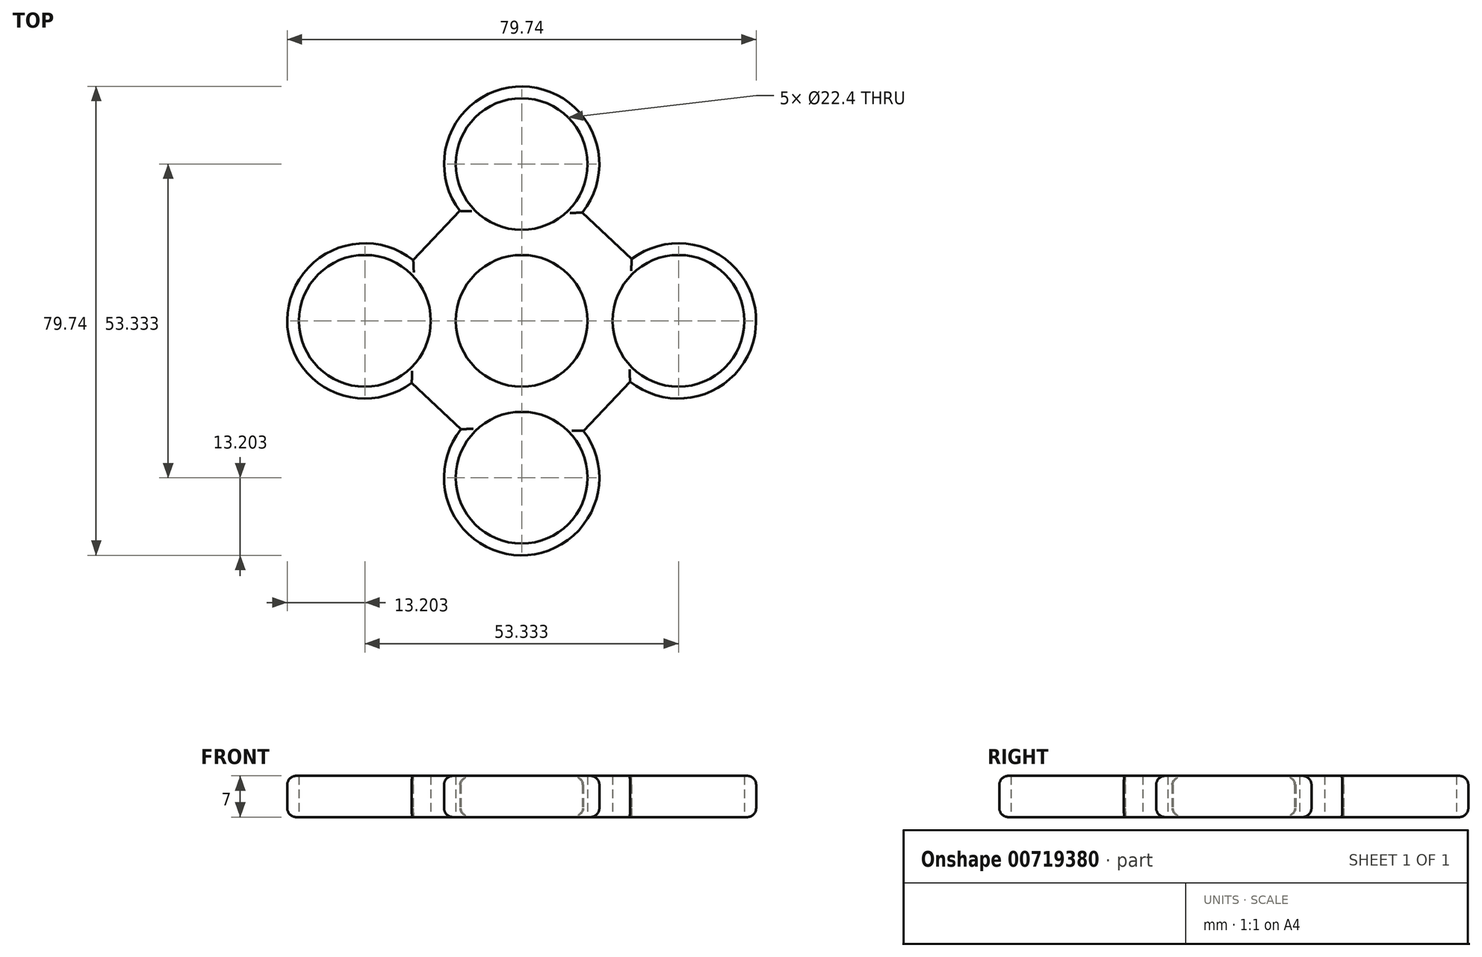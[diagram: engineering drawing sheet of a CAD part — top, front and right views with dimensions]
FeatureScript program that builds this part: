
annotation { "Feature Type Name" : "Feature", "Feature Type Description" : "" }
export const myFeature = defineFeature(function(context is Context, id is Id, definition is map)
    precondition{}
    {
        {
            var Q0;
            Q0=qCreatedBy(makeId("Top.planeOp"),FACE);
            var sketch = newSketch(context, id + "F0", { "sketchPlane" : qUnion([Q0])});
            skCircle(sketch, "E0", {"center": v(0, 0) * mm, "radius": 11.2 * mm});
            skCircle(sketch, "E1", {"center": v(0, 26.67) * mm, "radius": 11.2 * mm});
            skArc(sketch, "E2", {"start": v(10.32, 18.44) * mm, "mid": v(0.17, 39.87) * mm, "end": v(-10.53, 18.7) * mm});
            skArc(sketch, "E3.1.0", {"start": v(-18.44, 10.32) * mm, "mid": v(-39.87, 0.17) * mm, "end": v(-18.7, -10.53) * mm});
            skCircle(sketch, "E3.1.1", {"center": v(-26.67, 0) * mm, "radius": 11.2 * mm});
            skArc(sketch, "E3.2.0", {"start": v(-10.32, -18.44) * mm, "mid": v(-0.17, -39.87) * mm, "end": v(10.53, -18.7) * mm});
            skCircle(sketch, "E3.2.1", {"center": v(0, -26.67) * mm, "radius": 11.2 * mm});
            skArc(sketch, "E3.3.0", {"start": v(18.44, -10.32) * mm, "mid": v(39.87, -0.17) * mm, "end": v(18.7, 10.53) * mm});
            skCircle(sketch, "E3.3.1", {"center": v(26.67, 0) * mm, "radius": 11.2 * mm});
            skLineSegment(sketch, "E4", {"start": v(10.32, 18.44) * mm, "end": v(18.7, 10.53) * mm});
            skLineSegment(sketch, "E5.1.0", {"start": v(-18.44, 10.32) * mm, "end": v(-10.53, 18.7) * mm});
            skLineSegment(sketch, "E5.2.0", {"start": v(-10.32, -18.44) * mm, "end": v(-18.7, -10.53) * mm});
            skLineSegment(sketch, "E5.3.0", {"start": v(18.44, -10.32) * mm, "end": v(10.53, -18.7) * mm});
            skSolve(sketch);
        }
        {
            var Q0;
            Q0=makeQuery(id+"F0.imprint","IMPRINT",FACE,{"disambiguationData":[TD([[makeQuery(id+"F0.imprint","IMPRINT",EDGE,{"derivedFrom":sQuery(id+"F0.wireOp",EDGE,"E0")}),-1.0]])]});
            extrude(context, id + "F1", {"entities" : qUnion([Q0]), "depth" : 7 * mm, "offsetDistance" : 25 * mm});
        }
        {
            var Q0;
            Q0=makeQuery(id+"F1.opExtrude","CAP_EDGE",EDGE,{"disambiguationData":[OSD([sQuery(id+"F0.wireOp",EDGE,"E5.3.0")])],"isStart":true});
            var Q1;
            Q1=makeQuery(id+"F1.opExtrude","CAP_EDGE",EDGE,{"disambiguationData":[OSD([sQuery(id+"F0.wireOp",EDGE,"E3.3.0")])],"isStart":true});
            var Q2;
            Q2=makeQuery(id+"F1.opExtrude","CAP_EDGE",EDGE,{"disambiguationData":[OSD([sQuery(id+"F0.wireOp",EDGE,"E4")])],"isStart":true});
            var Q3;
            Q3=makeQuery(id+"F1.opExtrude","CAP_EDGE",EDGE,{"disambiguationData":[OSD([sQuery(id+"F0.wireOp",EDGE,"E2")])],"isStart":true});
            var Q4;
            Q4=makeQuery(id+"F1.opExtrude","CAP_EDGE",EDGE,{"disambiguationData":[OSD([sQuery(id+"F0.wireOp",EDGE,"E5.1.0")])],"isStart":true});
            var Q5;
            Q5=makeQuery(id+"F1.opExtrude","CAP_EDGE",EDGE,{"disambiguationData":[OSD([sQuery(id+"F0.wireOp",EDGE,"E3.1.0")])],"isStart":true});
            var Q6;
            Q6=makeQuery(id+"F1.opExtrude","CAP_EDGE",EDGE,{"disambiguationData":[OSD([sQuery(id+"F0.wireOp",EDGE,"E5.2.0")])],"isStart":true});
            var Q7;
            Q7=makeQuery(id+"F1.opExtrude","CAP_EDGE",EDGE,{"disambiguationData":[OSD([sQuery(id+"F0.wireOp",EDGE,"E3.2.0")])],"isStart":true});
            fillet(context, id + "F2", {"entities" : qUnion([Q0, Q1, Q2, Q3, Q4, Q5, Q6, Q7]), "radius" : 1.5 * mm, "tangentPropagation" : true, "allowEdgeOverflow" : false});
        }
        {
            var Q0;
            Q0=makeQuery(id+"F1.opExtrude","CAP_EDGE",EDGE,{"disambiguationData":[OSD([sQuery(id+"F0.wireOp",EDGE,"E2")])],"isStart":false});
            var Q1;
            Q1=makeQuery(id+"F1.opExtrude","CAP_EDGE",EDGE,{"disambiguationData":[OSD([sQuery(id+"F0.wireOp",EDGE,"E4")])],"isStart":false});
            var Q2;
            Q2=makeQuery(id+"F1.opExtrude","CAP_EDGE",EDGE,{"disambiguationData":[OSD([sQuery(id+"F0.wireOp",EDGE,"E3.3.0")])],"isStart":false});
            var Q3;
            Q3=makeQuery(id+"F1.opExtrude","CAP_EDGE",EDGE,{"disambiguationData":[OSD([sQuery(id+"F0.wireOp",EDGE,"E5.3.0")])],"isStart":false});
            var Q4;
            Q4=makeQuery(id+"F1.opExtrude","CAP_EDGE",EDGE,{"disambiguationData":[OSD([sQuery(id+"F0.wireOp",EDGE,"E3.2.0")])],"isStart":false});
            var Q5;
            Q5=makeQuery(id+"F1.opExtrude","CAP_EDGE",EDGE,{"disambiguationData":[OSD([sQuery(id+"F0.wireOp",EDGE,"E5.2.0")])],"isStart":false});
            var Q6;
            Q6=makeQuery(id+"F1.opExtrude","CAP_EDGE",EDGE,{"disambiguationData":[OSD([sQuery(id+"F0.wireOp",EDGE,"E3.1.0")])],"isStart":false});
            var Q7;
            Q7=makeQuery(id+"F1.opExtrude","CAP_EDGE",EDGE,{"disambiguationData":[OSD([sQuery(id+"F0.wireOp",EDGE,"E5.1.0")])],"isStart":false});
            fillet(context, id + "F3", {"entities" : qUnion([Q0, Q1, Q2, Q3, Q4, Q5, Q6, Q7]), "radius" : 1.5 * mm, "tangentPropagation" : true, "allowEdgeOverflow" : false});
        }
    });
